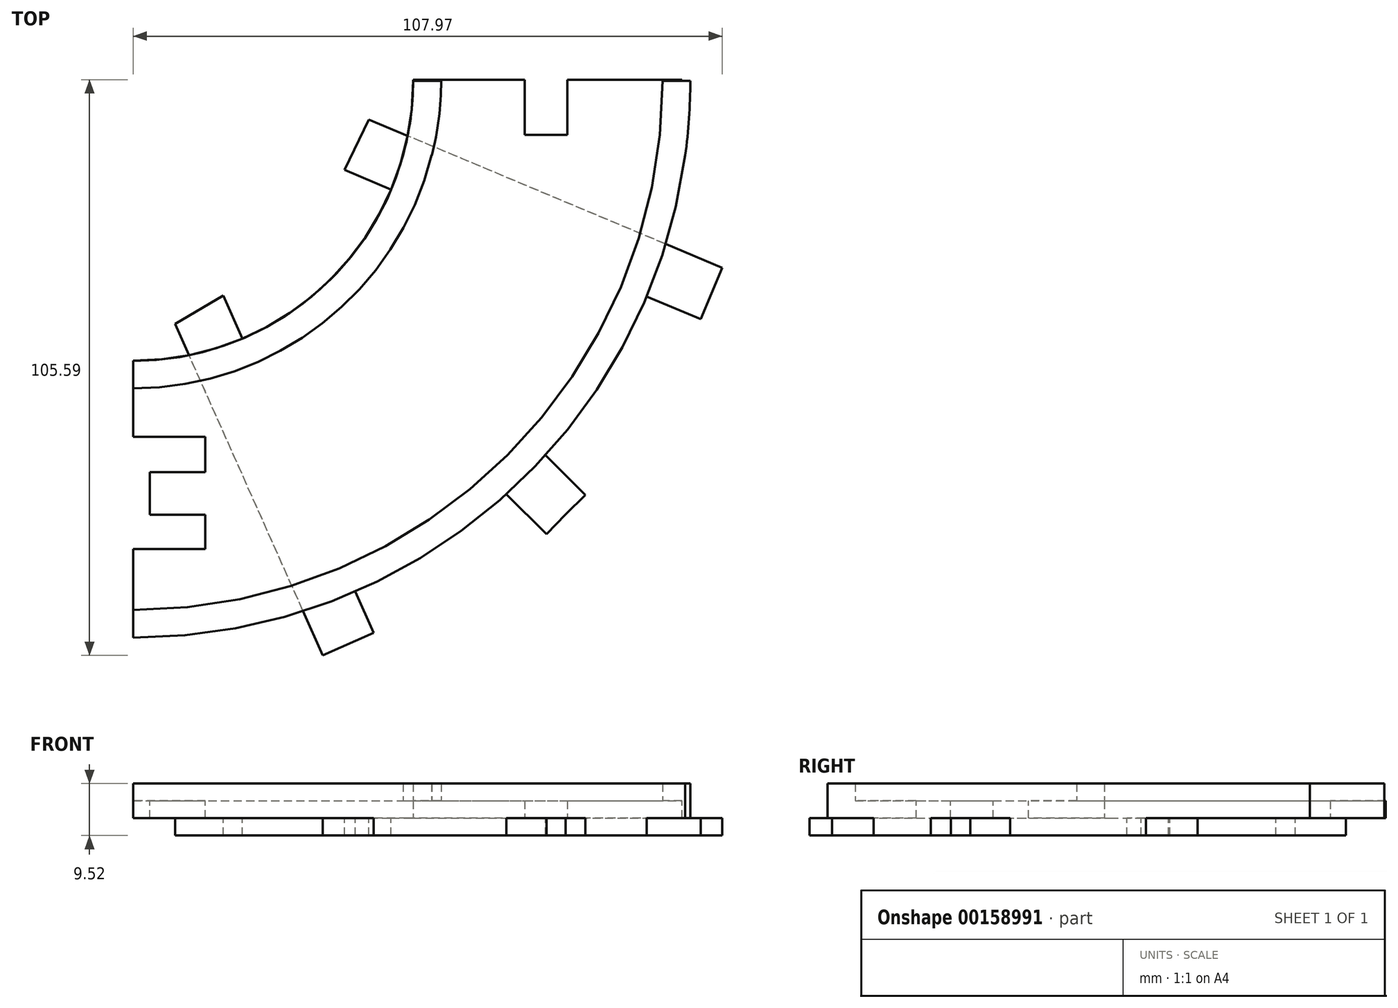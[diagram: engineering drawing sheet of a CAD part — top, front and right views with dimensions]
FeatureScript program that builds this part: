
annotation { "Feature Type Name" : "Feature", "Feature Type Description" : "" }
export const myFeature = defineFeature(function(context is Context, id is Id, definition is map)
    precondition{}
    {
        {
            var Q0;
            Q0=qCreatedBy(makeId("Top.planeOp"),FACE);
            var sketch = newSketch(context, id + "F0", { "sketchPlane" : qUnion([Q0])});
            skCircle(sketch, "E0", {"center": v(0, 0) * mm, "radius": 102.1 * mm});
            skCircle(sketch, "E1", {"center": v(0, 0) * mm, "radius": 51.3 * mm});
            skLineSegment(sketch, "E2", {"start": v(102.1, 0) * mm, "end": v(51.24, 0) * mm});
            skLineSegment(sketch, "E3", {"start": v(0, -51.3) * mm, "end": v(0, -102.1) * mm});
            skLineSegment(sketch, "E4", {"start": v(0, -102.1) * mm, "end": v(-44.33, -102.1) * mm});
            skLineSegment(sketch, "E5", {"start": v(-44.33, -102.1) * mm, "end": v(-44.33, -51.3) * mm});
            skLineSegment(sketch, "E6", {"start": v(-44.33, -51.3) * mm, "end": v(0, -51.3) * mm});
            skLineSegment(sketch, "E7", {"start": v(-16.74, -51.3) * mm, "end": v(-16.74, -102.1) * mm});
            skSolve(sketch);
        }
        {
            var Q0;
            {var subQ3=sQuery(id+"F0.wireOp",EDGE,"E3");Q0=makeQuery(id+"F0.imprint","IMPRINT",FACE,{"disambiguationData":[TD([[makeQuery(id+"F0.imprint","IMPRINT",EDGE,{"derivedFrom":subQ3}),1.0]])]});}
            extrude(context, id + "F1", {"entities" : qUnion([Q0]), "depth" : 3.17 * mm});
        }
        {
            var Q0;
            Q0=qCreatedBy(makeId("Top.planeOp"),FACE);
            var sketch = newSketch(context, id + "F2", { "sketchPlane" : qUnion([Q0])});
            skLineSegment(sketch, "E8", {"start": v(79.58, -6.3) * mm, "end": v(79.58, -9.91) * mm});
            skLineSegment(sketch, "E9", {"start": v(79.58, -9.91) * mm, "end": v(71.79, -9.91) * mm});
            skLineSegment(sketch, "E10", {"start": v(71.79, -9.91) * mm, "end": v(71.79, -6.3) * mm});
            skLineSegment(sketch, "E11", {"start": v(65.39, 0.24) * mm, "end": v(65.39, -13.41) * mm});
            skLineSegment(sketch, "E12", {"start": v(75.68, -13.41) * mm, "end": v(65.39, -13.41) * mm});
            skLineSegment(sketch, "E13", {"start": v(85.96, -13.41) * mm, "end": v(75.68, -13.41) * mm});
            skLineSegment(sketch, "E14", {"start": v(85.96, -13.41) * mm, "end": v(85.9, 0.24) * mm});
            skLineSegment(sketch, "E15", {"start": v(85.9, 0.24) * mm, "end": v(65.39, 0.24) * mm});
            skLineSegment(sketch, "E16", {"start": v(71.79, -6.3) * mm, "end": v(71.79, 0.24) * mm});
            skLineSegment(sketch, "E17", {"start": v(79.58, -6.3) * mm, "end": v(79.58, 0.24) * mm});
            skLineSegment(sketch, "E18", {"start": v(85.9, 0.24) * mm, "end": v(100.59, 0.24) * mm});
            skLineSegment(sketch, "E19", {"start": v(100.59, 0.24) * mm, "end": v(100.59, -13.41) * mm});
            skLineSegment(sketch, "E20", {"start": v(100.59, -13.41) * mm, "end": v(85.96, -13.41) * mm});
            skLineSegment(sketch, "E21", {"start": v(101.17, 0) * mm, "end": v(101.17, 0) * mm});
            skLineSegment(sketch, "E22", {"start": v(-6.04, -13.67) * mm, "end": v(65.39, -13.41) * mm});
            skLineSegment(sketch, "E23", {"start": v(51.3, -27.3) * mm, "end": v(51.3, 0.24) * mm});
            skLineSegment(sketch, "E24", {"start": v(51.3, 0.24) * mm, "end": v(65.39, 0.24) * mm});
            skLineSegment(sketch, "E25", {"start": v(100.59, 0.24) * mm, "end": v(104.76, 0.24) * mm});
            skLineSegment(sketch, "E26", {"start": v(104.76, 0.24) * mm, "end": v(104.76, -13.41) * mm});
            skLineSegment(sketch, "E27", {"start": v(104.76, -13.41) * mm, "end": v(100.59, -13.41) * mm});
            skSolve(sketch);
        }
        {
            var Q0;
            Q0=makeQuery(id+"FCGjtFl4DsFHXbu_1.boolean.opBoolean","MERGE",FACE,{"derivedFrom":[makeQuery(id+"F1.opExtrude","CAP_FACE",FACE,{"disambiguationData":[OSD([sQuery(id+"F0.wireOp",EDGE,"E0"),sQuery(id+"F0.wireOp",EDGE,"E1"),sQuery(id+"F0.wireOp",EDGE,"E2"),sQuery(id+"F0.wireOp",EDGE,"E3")])],"isStart":false}),makeQuery(id+"FCGjtFl4DsFHXbu_1.opExtrude","CAP_FACE",FACE,{"disambiguationData":[OSD([sQuery(id+"F2.wireOp",EDGE,"ecf8c89f-ef39-4beb-ab77-ea36b8de9ece"),sQuery(id+"F2.wireOp",EDGE,"E8"),sQuery(id+"F2.wireOp",EDGE,"E9"),sQuery(id+"F2.wireOp",EDGE,"E10"),sQuery(id+"F2.wireOp",EDGE,"bec0f09a-aca4-4be2-b8df-57b3bef6ff18"),sQuery(id+"F2.wireOp",EDGE,"E15"),sQuery(id+"F2.wireOp",EDGE,"E16"),sQuery(id+"F2.wireOp",EDGE,"E17")])],"isStart":false}),makeQuery(id+"FCGjtFl4DsFHXbu_1.opExtrude","CAP_FACE",FACE,{"disambiguationData":[OSD([sQuery(id+"F2.wireOp",EDGE,"E11"),sQuery(id+"F2.wireOp",EDGE,"HhnOl6Ur-7oBW-enPF-9H80-fVUDD1N4fKMp"),sQuery(id+"F2.wireOp",EDGE,"E21"),sQuery(id+"F2.wireOp",EDGE,"E22")])],"isStart":false}),makeQuery(id+"FCGjtFl4DsFHXbu_1.opExtrude","CAP_FACE",FACE,{"disambiguationData":[OSD([sQuery(id+"F2.wireOp",EDGE,"E14"),sQuery(id+"F2.wireOp",EDGE,"E18"),sQuery(id+"F2.wireOp",EDGE,"E19"),sQuery(id+"F2.wireOp",EDGE,"E20")])],"isStart":false})]});
            var sketch = newSketch(context, id + "F3", { "sketchPlane" : qUnion([Q0])});
            skCircle(sketch, "E28", {"center": v(0, 0) * mm, "radius": 56.38 * mm});
            skCircle(sketch, "E29", {"center": v(0, 0) * mm, "radius": 97.01 * mm});
            skCircle(sketch, "E30", {"center": v(0, 0) * mm, "radius": 51.33 * mm});
            skCircle(sketch, "E31", {"center": v(0, 0) * mm, "radius": 102.28 * mm});
            skLineSegment(sketch, "E32", {"start": v(0, 0) * mm, "end": v(0, -102.1) * mm});
            skLineSegment(sketch, "E33", {"start": v(0, 0) * mm, "end": v(102.1, 0) * mm});
            skSolve(sketch);
        }
        {
            var Q0;
            {var subQ0=sQuery(id+"F3.wireOp",EDGE,"E33");var subQ1=sQuery(id+"F3.wireOp",EDGE,"E28");var subQ2=makeQuery(id+"F3.imprint","INTERSECT",VERTEX,{"derivedFrom":[subQ1,subQ0]});Q0=makeQuery(id+"F3.imprint","IMPRINT",FACE,{"disambiguationData":[TD([[makeQuery(id+"F3.imprint","IMPRINT",EDGE,{"disambiguationData":[TD([[subQ2,1.0]])],"derivedFrom":subQ1}),1.0]])]});}
            var Q1;
            {var subQ4=makeQuery(id+"F1.opExtrude","CAP_EDGE",EDGE,{"disambiguationData":[OSD([sQuery(id+"F0.wireOp",EDGE,"E0")])],"isStart":false});Q1=makeQuery(id+"F3.imprint","IMPRINT",FACE,{"disambiguationData":[TD([[makeQuery(id+"F3.imprint","IMPRINT",EDGE,{"derivedFrom":subQ4}),1.0]])]});}
            extrude(context, id + "F4", {"entities" : qUnion([Q0, Q1]), "operationType" : NewBodyOperationType.ADD, "depth" : 3.17 * mm});
        }
        {
            var Q0;
            Q0=qCreatedBy(makeId("Top.planeOp"),FACE);
            var sketch = newSketch(context, id + "F5", { "sketchPlane" : qUnion([Q0])});
            skCircle(sketch, "E34", {"center": v(0, 0) * mm, "radius": 56.44 * mm});
            skCircle(sketch, "E35", {"center": v(0, 0) * mm, "radius": 51.3 * mm});
            skCircle(sketch, "E36", {"center": v(0, 0) * mm, "radius": 102.1 * mm});
            skCircle(sketch, "E37", {"center": v(0, 0) * mm, "radius": 97.14 * mm});
            skLineSegment(sketch, "E38", {"start": v(0, 0) * mm, "end": v(102.1, 0) * mm});
            skLineSegment(sketch, "E39", {"start": v(0, 0) * mm, "end": v(0, -102.1) * mm});
            skLineSegment(sketch, "E40", {"start": v(49.45, -13.66) * mm, "end": v(101.19, -13.66) * mm});
            skSolve(sketch);
        }
        {
            var Q0;
            {var subQ0=sQuery(id+"F5.wireOp",EDGE,"E38");var subQ1=sQuery(id+"F5.wireOp",EDGE,"E34");var subQ2=makeQuery(id+"F5.imprint","INTERSECT",VERTEX,{"derivedFrom":[subQ1,subQ0]});Q0=makeQuery(id+"F5.imprint","IMPRINT",FACE,{"disambiguationData":[TD([[makeQuery(id+"F5.imprint","IMPRINT",EDGE,{"disambiguationData":[TD([[subQ2,1.0]])],"derivedFrom":subQ1}),1.0]])]});}
            var Q1;
            {var subQ0=sQuery(id+"F5.wireOp",EDGE,"E38");var subQ1=sQuery(id+"F5.wireOp",EDGE,"E36");var subQ2=makeQuery(id+"F5.imprint","INTERSECT",VERTEX,{"derivedFrom":[subQ1,subQ0]});Q1=makeQuery(id+"F5.imprint","IMPRINT",FACE,{"disambiguationData":[TD([[makeQuery(id+"F5.imprint","IMPRINT",EDGE,{"disambiguationData":[TD([[subQ2,1.0]])],"derivedFrom":subQ1}),1.0]])]});}
            extrude(context, id + "F6", {"entities" : qUnion([Q0, Q1]), "operationType" : NewBodyOperationType.ADD, "depth" : 6.35 * mm});
        }
        {
            var Q0;
            Q0=makeQuery(id+"F2.imprint","IMPRINT",FACE,{"disambiguationData":[TD([[makeQuery(id+"F2.imprint","IMPRINT",EDGE,{"derivedFrom":sQuery(id+"F2.wireOp",EDGE,"E11")}),-1.0]])]});
            var Q1;
            Q1=makeQuery(id+"F2.imprint","IMPRINT",FACE,{"disambiguationData":[TD([[makeQuery(id+"F2.imprint","IMPRINT",EDGE,{"derivedFrom":sQuery(id+"F2.wireOp",EDGE,"E14")}),-1.0]])]});
            extrude(context, id + "F7", {"entities" : qUnion([Q0, Q1]), "operationType" : NewBodyOperationType.ADD, "depth" : 3.17 * mm});
        }
        {
            var Q0;
            {var subQ1=sQuery(id+"F3.wireOp",EDGE,"E28");var subQ2=sQuery(id+"F0.wireOp",EDGE,"E3");var subQ5=sQuery(id+"F0.wireOp",EDGE,"E2");var subQ7=sQuery(id+"F0.wireOp",EDGE,"E0");Q0=makeQuery(id+"F7.boolean.opBoolean","MERGE",FACE,{"derivedFrom":[makeQuery(id+"F4.boolean.opBoolean","SPLIT",FACE,{"disambiguationData":[TD([makeQuery(id+"F4.opExtrude","SWEPT_FACE",FACE,{"disambiguationData":[OSD([subQ1])]})])],"derivedFrom":makeQuery(id+"F1.opExtrude","CAP_FACE",FACE,{"disambiguationData":[OSD([subQ7,sQuery(id+"F0.wireOp",EDGE,"E1"),subQ5,subQ2])],"isStart":false})}),makeQuery(id+"F7.opExtrude","CAP_FACE",FACE,{"disambiguationData":[OSD([sQuery(id+"F2.wireOp",EDGE,"E11"),sQuery(id+"F2.wireOp",EDGE,"E22"),sQuery(id+"F2.wireOp",EDGE,"E23"),sQuery(id+"F2.wireOp",EDGE,"E24")])],"isStart":false}),makeQuery(id+"F7.opExtrude","CAP_FACE",FACE,{"disambiguationData":[OSD([sQuery(id+"F2.wireOp",EDGE,"E14"),sQuery(id+"F2.wireOp",EDGE,"E18"),sQuery(id+"F2.wireOp",EDGE,"E19"),sQuery(id+"F2.wireOp",EDGE,"E20")])],"isStart":false})]});}
            var sketch = newSketch(context, id + "F8", { "sketchPlane" : qUnion([Q0])});
            skLineSegment(sketch, "E41.top", {"start": v(13.23, -101.1) * mm, "end": v(13.23, -50.3) * mm});
            skLineSegment(sketch, "E42", {"start": v(13.23, -86) * mm, "end": v(13.23, -79.51) * mm});
            skLineSegment(sketch, "E43", {"start": v(13.23, -79.51) * mm, "end": v(6.76, -79.51) * mm});
            skLineSegment(sketch, "E44", {"start": v(6.76, -79.51) * mm, "end": v(3.06, -79.51) * mm});
            skLineSegment(sketch, "E45", {"start": v(3.06, -79.51) * mm, "end": v(3.06, -71.72) * mm});
            skLineSegment(sketch, "E46", {"start": v(3.06, -71.72) * mm, "end": v(6.76, -71.72) * mm});
            skLineSegment(sketch, "E47", {"start": v(6.76, -71.72) * mm, "end": v(13.23, -71.72) * mm});
            skLineSegment(sketch, "E48", {"start": v(13.23, -71.72) * mm, "end": v(13.23, -65.25) * mm});
            skLineSegment(sketch, "E49", {"start": v(13.23, -65.25) * mm, "end": v(-0.42, -65.25) * mm});
            skLineSegment(sketch, "E50", {"start": v(-0.42, -75.54) * mm, "end": v(-0.42, -65.25) * mm});
            skLineSegment(sketch, "E51", {"start": v(-0.42, -85.83) * mm, "end": v(-0.42, -75.54) * mm});
            skLineSegment(sketch, "E52", {"start": v(-0.42, -85.83) * mm, "end": v(13.23, -85.83) * mm});
            skLineSegment(sketch, "E53", {"start": v(13.23, -85.83) * mm, "end": v(13.23, -65.25) * mm});
            skLineSegment(sketch, "E54", {"start": v(-0.42, -85.83) * mm, "end": v(-0.42, -101.1) * mm});
            skLineSegment(sketch, "E55", {"start": v(-0.42, -101.1) * mm, "end": v(-0.42, -65.25) * mm});
            skLineSegment(sketch, "E56", {"start": v(-0.42, -65.25) * mm, "end": v(-0.42, -50.3) * mm});
            skLineSegment(sketch, "E57", {"start": v(-0.42, -101.1) * mm, "end": v(13.23, -101.1) * mm});
            skLineSegment(sketch, "E58", {"start": v(-0.42, -50.3) * mm, "end": v(13.23, -50.3) * mm});
            skSolve(sketch);
        }
        {
            var Q0;
            {var subQ10=sQuery(id+"F8.wireOp",EDGE,"E43");Q0=makeQuery(id+"F8.imprint","IMPRINT",FACE,{"disambiguationData":[TD([[makeQuery(id+"F8.imprint","IMPRINT",EDGE,{"derivedFrom":subQ10}),1.0]])]});}
            extrude(context, id + "F9", {"entities" : qUnion([Q0]), "operationType" : NewBodyOperationType.REMOVE, "oppositeDirection" : true, "depth" : 25.4 * mm});
        }
        {
            var Q0;
            {var subQ0=sQuery(id+"F5.wireOp",EDGE,"E40");var subQ1=sQuery(id+"F5.wireOp",EDGE,"E38");Q0=makeQuery(id+"F7.boolean.opBoolean","MERGE",FACE,{"derivedFrom":[makeQuery(id+"F6.boolean.opBoolean","MERGE",FACE,{"derivedFrom":[makeQuery(id+"F1.opExtrude","CAP_FACE",FACE,{"disambiguationData":[OSD([sQuery(id+"F0.wireOp",EDGE,"E0"),sQuery(id+"F0.wireOp",EDGE,"E1"),sQuery(id+"F0.wireOp",EDGE,"E2"),sQuery(id+"F0.wireOp",EDGE,"E3")])],"isStart":true}),makeQuery(id+"F6.opExtrude","CAP_FACE",FACE,{"disambiguationData":[OSD([sQuery(id+"F5.wireOp",EDGE,"E34"),sQuery(id+"F5.wireOp",EDGE,"E35"),subQ1,subQ0])],"isStart":true}),makeQuery(id+"F6.opExtrude","CAP_FACE",FACE,{"disambiguationData":[OSD([sQuery(id+"F5.wireOp",EDGE,"E36"),sQuery(id+"F5.wireOp",EDGE,"E37"),subQ1,subQ0])],"isStart":true})]}),makeQuery(id+"F7.opExtrude","CAP_FACE",FACE,{"disambiguationData":[OSD([sQuery(id+"F2.wireOp",EDGE,"E11"),sQuery(id+"F2.wireOp",EDGE,"E22"),sQuery(id+"F2.wireOp",EDGE,"E23"),sQuery(id+"F2.wireOp",EDGE,"E24")])],"isStart":true}),makeQuery(id+"F7.opExtrude","CAP_FACE",FACE,{"disambiguationData":[OSD([sQuery(id+"F2.wireOp",EDGE,"E14"),sQuery(id+"F2.wireOp",EDGE,"E18"),sQuery(id+"F2.wireOp",EDGE,"E19"),sQuery(id+"F2.wireOp",EDGE,"E20")])],"isStart":true})]});}
            var sketch = newSketch(context, id + "F10", { "sketchPlane" : qUnion([Q0])});
            skLineSegment(sketch, "E59", {"start": v(72.1, 72.28) * mm, "end": v(0, 0) * mm});
            skLineSegment(sketch, "E60", {"start": v(72.1, 72.28) * mm, "end": v(79.27, 79.48) * mm});
            skLineSegment(sketch, "E61", {"start": v(36.22, 36.32) * mm, "end": v(29.05, 29.12) * mm});
            skLineSegment(sketch, "E62", {"start": v(29.05, 29.12) * mm, "end": v(25.45, 32.71) * mm});
            skLineSegment(sketch, "E63", {"start": v(29.05, 29.12) * mm, "end": v(32.65, 25.54) * mm});
            skLineSegment(sketch, "E64", {"start": v(25.45, 32.71) * mm, "end": v(75.73, 83.12) * mm});
            skLineSegment(sketch, "E65", {"start": v(75.73, 83.12) * mm, "end": v(79.27, 79.48) * mm});
            skLineSegment(sketch, "E66", {"start": v(32.65, 25.54) * mm, "end": v(82.88, 75.9) * mm});
            skLineSegment(sketch, "E67", {"start": v(82.88, 75.9) * mm, "end": v(79.27, 79.48) * mm});
            skLineSegment(sketch, "E68", {"start": v(25.45, 32.71) * mm, "end": v(16.52, 39.32) * mm});
            skLineSegment(sketch, "E69", {"start": v(32.65, 25.54) * mm, "end": v(38.71, 16.31) * mm});
            skLineSegment(sketch, "E70", {"start": v(38.71, 16.31) * mm, "end": v(104.01, 43.7) * mm});
            skLineSegment(sketch, "E71", {"start": v(104.01, 43.7) * mm, "end": v(107.97, 34.26) * mm});
            skLineSegment(sketch, "E72", {"start": v(107.97, 34.26) * mm, "end": v(43.16, 7.08) * mm});
            skLineSegment(sketch, "E73", {"start": v(43.16, 7.08) * mm, "end": v(38.71, 16.31) * mm});
            skLineSegment(sketch, "E74", {"start": v(16.52, 39.32) * mm, "end": v(44.06, 101.21) * mm});
            skLineSegment(sketch, "E75", {"start": v(44.06, 101.21) * mm, "end": v(34.76, 105.35) * mm});
            skLineSegment(sketch, "E76", {"start": v(34.76, 105.35) * mm, "end": v(7.71, 44.58) * mm});
            skLineSegment(sketch, "E77", {"start": v(7.71, 44.58) * mm, "end": v(16.52, 39.32) * mm});
            skSolve(sketch);
        }
        {
            var Q0;
            {var subQ0=sQuery(id+"F10.wireOp",EDGE,"E61");Q0=makeQuery(id+"F10.imprint","IMPRINT",FACE,{"disambiguationData":[TD([[makeQuery(id+"F10.imprint","IMPRINT",EDGE,{"derivedFrom":subQ0}),1.0]])]});}
            var Q1;
            {var subQ0=sQuery(id+"F10.wireOp",EDGE,"E61");Q1=makeQuery(id+"F10.imprint","IMPRINT",FACE,{"disambiguationData":[TD([[makeQuery(id+"F10.imprint","IMPRINT",EDGE,{"derivedFrom":subQ0}),-1.0]])]});}
            var Q2;
            {var subQ1=makeQuery(id+"F1.opExtrude","CAP_EDGE",EDGE,{"disambiguationData":[OSD([sQuery(id+"F0.wireOp",EDGE,"E0")])],"isStart":true});var subQ5=sQuery(id+"F10.wireOp",EDGE,"E64");var subQ6=makeQuery(id+"F10.imprint","INTERSECT",VERTEX,{"derivedFrom":[subQ1,subQ5]});Q2=makeQuery(id+"F10.imprint","IMPRINT",FACE,{"disambiguationData":[TD([[makeQuery(id+"F10.imprint","IMPRINT",EDGE,{"disambiguationData":[TD([[subQ6,1.0]])],"derivedFrom":subQ5}),-1.0]])]});}
            var Q3;
            {var subQ1=makeQuery(id+"F1.opExtrude","CAP_EDGE",EDGE,{"disambiguationData":[OSD([sQuery(id+"F0.wireOp",EDGE,"E0")])],"isStart":true});var subQ5=sQuery(id+"F10.wireOp",EDGE,"E66");var subQ6=makeQuery(id+"F10.imprint","INTERSECT",VERTEX,{"derivedFrom":[subQ1,subQ5]});Q3=makeQuery(id+"F10.imprint","IMPRINT",FACE,{"disambiguationData":[TD([[makeQuery(id+"F10.imprint","IMPRINT",EDGE,{"disambiguationData":[TD([[subQ6,1.0]])],"derivedFrom":subQ5}),1.0]])]});}
            var Q4;
            {var subQ0=sQuery(id+"F10.wireOp",EDGE,"E60");Q4=makeQuery(id+"F10.imprint","IMPRINT",FACE,{"disambiguationData":[TD([[makeQuery(id+"F10.imprint","IMPRINT",EDGE,{"derivedFrom":subQ0}),-1.0]])]});}
            var Q5;
            {var subQ0=sQuery(id+"F10.wireOp",EDGE,"E60");Q5=makeQuery(id+"F10.imprint","IMPRINT",FACE,{"disambiguationData":[TD([[makeQuery(id+"F10.imprint","IMPRINT",EDGE,{"derivedFrom":subQ0}),1.0]])]});}
            var Q6;
            {var subQ0=sQuery(id+"F10.wireOp",EDGE,"E74");var subQ1=makeQuery(id+"F1.opExtrude","CAP_EDGE",EDGE,{"disambiguationData":[OSD([sQuery(id+"F0.wireOp",EDGE,"E0")])],"isStart":true});var subQ2=makeQuery(id+"F10.imprint","INTERSECT",VERTEX,{"derivedFrom":[subQ1,subQ0]});Q6=makeQuery(id+"F10.imprint","IMPRINT",FACE,{"disambiguationData":[TD([[makeQuery(id+"F10.imprint","IMPRINT",EDGE,{"disambiguationData":[TD([[subQ2,1.0]])],"derivedFrom":subQ0}),1.0]])]});}
            var Q7;
            {var subQ0=sQuery(id+"F10.wireOp",EDGE,"E75");Q7=makeQuery(id+"F10.imprint","IMPRINT",FACE,{"disambiguationData":[TD([[makeQuery(id+"F10.imprint","IMPRINT",EDGE,{"derivedFrom":subQ0}),1.0]])]});}
            var Q8;
            {var subQ0=sQuery(id+"F10.wireOp",EDGE,"E77");Q8=makeQuery(id+"F10.imprint","IMPRINT",FACE,{"disambiguationData":[TD([[makeQuery(id+"F10.imprint","IMPRINT",EDGE,{"derivedFrom":subQ0}),1.0]])]});}
            var Q9;
            {var subQ8=sQuery(id+"F10.wireOp",EDGE,"E73");Q9=makeQuery(id+"F10.imprint","IMPRINT",FACE,{"disambiguationData":[TD([[makeQuery(id+"F10.imprint","IMPRINT",EDGE,{"derivedFrom":subQ8}),-1.0]])]});}
            var Q10;
            {var subQ7=sQuery(id+"F0.wireOp",EDGE,"E0");var subQ10=sQuery(id+"F10.wireOp",EDGE,"E70");var subQ13=makeQuery(id+"F1.opExtrude","CAP_EDGE",EDGE,{"disambiguationData":[OSD([subQ7])],"isStart":true});var subQ17=makeQuery(id+"F10.imprint","INTERSECT",VERTEX,{"derivedFrom":[subQ13,subQ10]});Q10=makeQuery(id+"F10.imprint","IMPRINT",FACE,{"disambiguationData":[TD([[makeQuery(id+"F10.imprint","IMPRINT",EDGE,{"disambiguationData":[TD([[subQ17,1.0]])],"derivedFrom":subQ10}),-1.0]])]});}
            var Q11;
            {var subQ0=sQuery(id+"F10.wireOp",EDGE,"E71");Q11=makeQuery(id+"F10.imprint","IMPRINT",FACE,{"disambiguationData":[TD([[makeQuery(id+"F10.imprint","IMPRINT",EDGE,{"derivedFrom":subQ0}),-1.0]])]});}
            extrude(context, id + "F11", {"entities" : qUnion([Q0, Q1, Q2, Q3, Q4, Q5, Q6, Q7, Q8, Q9, Q10, Q11]), "operationType" : NewBodyOperationType.ADD, "depth" : 3.17 * mm});
        }
        {
            var Q0;
            {var subQ0=sQuery(id+"F5.wireOp",EDGE,"E40");var subQ1=sQuery(id+"F5.wireOp",EDGE,"E36");var subQ2=sQuery(id+"F5.wireOp",EDGE,"E37");var subQ3=sQuery(id+"F0.wireOp",EDGE,"E0");var subQ6=sQuery(id+"F5.wireOp",EDGE,"E38");var subQ7=sQuery(id+"F0.wireOp",EDGE,"E2");var subQ8=makeQuery(id+"F1.opExtrude","SWEPT_FACE",FACE,{"disambiguationData":[OSD([subQ7])]});var subQ9=sQuery(id+"F2.wireOp",EDGE,"E11");var subQ10=sQuery(id+"F2.wireOp",EDGE,"E20");var subQ12=sQuery(id+"F2.wireOp",EDGE,"E18");var subQ17=makeQuery(id+"F1.opExtrude","SWEPT_FACE",FACE,{"disambiguationData":[OSD([subQ3])]});var subQ18=sQuery(id+"F0.wireOp",EDGE,"E1");var subQ23=sQuery(id+"F2.wireOp",EDGE,"E14");var subQ24=sQuery(id+"F2.wireOp",EDGE,"E19");var subQ25=sQuery(id+"F2.wireOp",EDGE,"E23");var subQ26=sQuery(id+"F2.wireOp",EDGE,"E24");var subQ27=sQuery(id+"F2.wireOp",EDGE,"E22");var subQ29=sQuery(id+"F0.wireOp",EDGE,"E3");Q0=makeQuery(id+"F11.boolean.opBoolean","SPLIT",FACE,{"disambiguationData":[TD([subQ8])],"derivedFrom":makeQuery(id+"F7.boolean.opBoolean","MERGE",FACE,{"derivedFrom":[makeQuery(id+"F6.boolean.opBoolean","MERGE",FACE,{"derivedFrom":[makeQuery(id+"Fei38nU6vnmVDr2_1.boolean.opBoolean","SPLIT",FACE,{"disambiguationData":[TD([subQ17])],"derivedFrom":makeQuery(id+"F1.opExtrude","CAP_FACE",FACE,{"disambiguationData":[OSD([subQ3,subQ18,subQ7,subQ29])],"isStart":true})}),makeQuery(id+"F6.opExtrude","CAP_FACE",FACE,{"disambiguationData":[OSD([sQuery(id+"F5.wireOp",EDGE,"E34"),sQuery(id+"F5.wireOp",EDGE,"E35"),subQ6,subQ0])],"isStart":true}),makeQuery(id+"F6.opExtrude","CAP_FACE",FACE,{"disambiguationData":[OSD([subQ1,subQ2,subQ6,subQ0])],"isStart":true})]}),makeQuery(id+"F7.opExtrude","CAP_FACE",FACE,{"disambiguationData":[OSD([subQ9,subQ27,subQ25,subQ26])],"isStart":true}),makeQuery(id+"F7.opExtrude","CAP_FACE",FACE,{"disambiguationData":[OSD([subQ23,subQ12,subQ24,subQ10])],"isStart":true})]})});}
            var sketch = newSketch(context, id + "F12", { "sketchPlane" : qUnion([Q0])});
            skLineSegment(sketch, "E78", {"start": v(65.39, -0.24) * mm, "end": v(85.9, -0.24) * mm});
            skSolve(sketch);
        }
        {
            var Q0;
            Q0=makeQuery(id+"F12.imprint","IMPRINT",FACE,{"disambiguationData":[TD([[makeQuery(id+"F12.imprint","IMPRINT",EDGE,{"derivedFrom":sQuery(id+"F12.wireOp",EDGE,"E78")}),1.0]])]});
            extrude(context, id + "F13", {"entities" : qUnion([Q0]), "operationType" : NewBodyOperationType.ADD, "oppositeDirection" : true, "depth" : 3.17 * mm});
        }
        {
            var Q0;
            {var subQ0=sQuery(id+"F0.wireOp",EDGE,"E0");var subQ1=sQuery(id+"F0.wireOp",EDGE,"E1");var subQ2=sQuery(id+"F10.wireOp",EDGE,"E66");Q0=makeQuery(id+"F11.boolean.opBoolean","SPLIT",FACE,{"disambiguationData":[TD([makeQuery(id+"F11.opExtrude","SWEPT_FACE",FACE,{"disambiguationData":[OSD([subQ2])]})])],"derivedFrom":makeQuery(id+"F7.boolean.opBoolean","MERGE",FACE,{"derivedFrom":[makeQuery(id+"F6.boolean.opBoolean","MERGE",FACE,{"derivedFrom":[makeQuery(id+"F1.opExtrude","CAP_FACE",FACE,{"disambiguationData":[OSD([subQ0,subQ1,sQuery(id+"F0.wireOp",EDGE,"E2"),sQuery(id+"F0.wireOp",EDGE,"E3")])],"isStart":true}),makeQuery(id+"F6.opExtrude","CAP_FACE",FACE,{"disambiguationData":[OSD([sQuery(id+"F5.wireOp",EDGE,"E36"),sQuery(id+"F5.wireOp",EDGE,"E37"),sQuery(id+"F5.wireOp",EDGE,"E38"),sQuery(id+"F5.wireOp",EDGE,"E40")])],"isStart":true})]}),makeQuery(id+"F7.opExtrude","CAP_FACE",FACE,{"disambiguationData":[OSD([sQuery(id+"F2.wireOp",EDGE,"E11"),sQuery(id+"F2.wireOp",EDGE,"E22"),sQuery(id+"F2.wireOp",EDGE,"E23"),sQuery(id+"F2.wireOp",EDGE,"E24")])],"isStart":true}),makeQuery(id+"F7.opExtrude","CAP_FACE",FACE,{"disambiguationData":[OSD([sQuery(id+"F2.wireOp",EDGE,"E14"),sQuery(id+"F2.wireOp",EDGE,"E18"),sQuery(id+"F2.wireOp",EDGE,"E19"),sQuery(id+"F2.wireOp",EDGE,"E20")])],"isStart":true})]})});}
            var Q1;
            {var subQ0=sQuery(id+"F0.wireOp",EDGE,"E0");var subQ1=sQuery(id+"F10.wireOp",EDGE,"E64");var subQ2=sQuery(id+"F0.wireOp",EDGE,"E1");Q1=makeQuery(id+"F11.boolean.opBoolean","SPLIT",FACE,{"disambiguationData":[TD([makeQuery(id+"F11.opExtrude","SWEPT_FACE",FACE,{"disambiguationData":[OSD([subQ1])]})])],"derivedFrom":makeQuery(id+"F7.boolean.opBoolean","MERGE",FACE,{"derivedFrom":[makeQuery(id+"F6.boolean.opBoolean","MERGE",FACE,{"derivedFrom":[makeQuery(id+"F1.opExtrude","CAP_FACE",FACE,{"disambiguationData":[OSD([subQ0,subQ2,sQuery(id+"F0.wireOp",EDGE,"E2"),sQuery(id+"F0.wireOp",EDGE,"E3")])],"isStart":true}),makeQuery(id+"F6.opExtrude","CAP_FACE",FACE,{"disambiguationData":[OSD([sQuery(id+"F5.wireOp",EDGE,"E36"),sQuery(id+"F5.wireOp",EDGE,"E37"),sQuery(id+"F5.wireOp",EDGE,"E38"),sQuery(id+"F5.wireOp",EDGE,"E40")])],"isStart":true})]}),makeQuery(id+"F7.opExtrude","CAP_FACE",FACE,{"disambiguationData":[OSD([sQuery(id+"F2.wireOp",EDGE,"E11"),sQuery(id+"F2.wireOp",EDGE,"E22"),sQuery(id+"F2.wireOp",EDGE,"E23"),sQuery(id+"F2.wireOp",EDGE,"E24")])],"isStart":true}),makeQuery(id+"F7.opExtrude","CAP_FACE",FACE,{"disambiguationData":[OSD([sQuery(id+"F2.wireOp",EDGE,"E14"),sQuery(id+"F2.wireOp",EDGE,"E18"),sQuery(id+"F2.wireOp",EDGE,"E19"),sQuery(id+"F2.wireOp",EDGE,"E20")])],"isStart":true})]})});}
            extrude(context, id + "F14", {"entities" : qUnion([Q0, Q1]), "operationType" : NewBodyOperationType.ADD, "depth" : 3.17 * mm});
        }
        {
            var Q0;
            Q0=makeQuery(id+"F2.imprint","IMPRINT",FACE,{"disambiguationData":[TD([[makeQuery(id+"F2.imprint","IMPRINT",EDGE,{"derivedFrom":sQuery(id+"F2.wireOp",EDGE,"E8")}),-1.0]])]});
            extrude(context, id + "F15", {"entities" : qUnion([Q0]), "operationType" : NewBodyOperationType.REMOVE, "endBound" : BoundingType.THROUGH_ALL, "depth" : 25.4 * mm});
        }
    });
